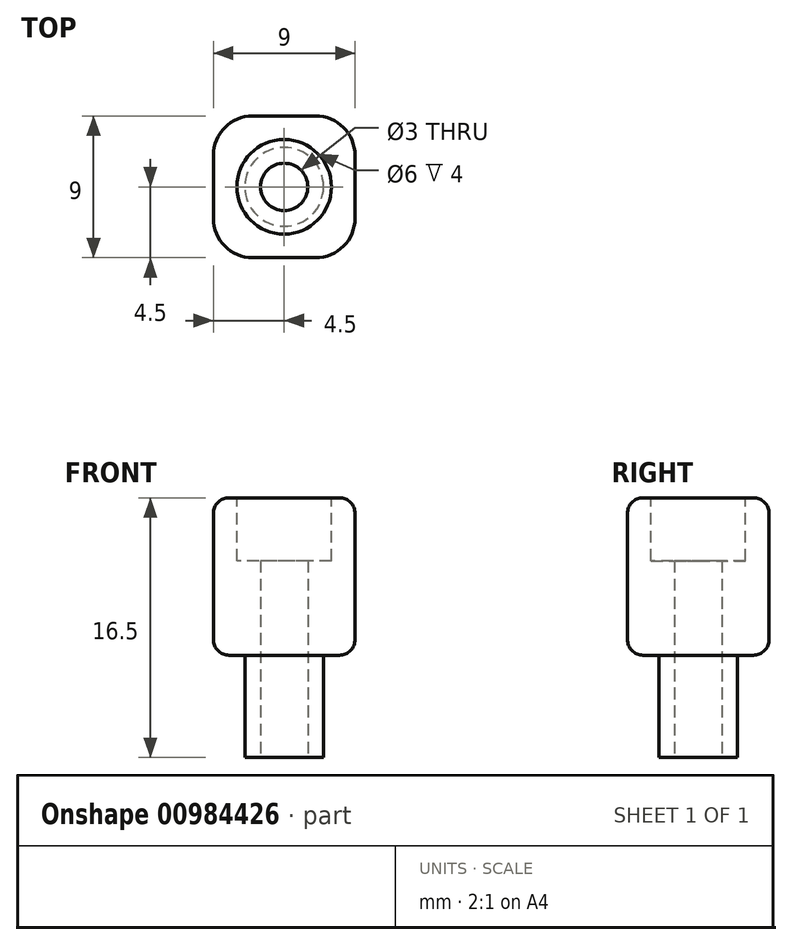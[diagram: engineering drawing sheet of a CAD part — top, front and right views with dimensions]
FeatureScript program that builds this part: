
annotation { "Feature Type Name" : "Feature", "Feature Type Description" : "" }
export const myFeature = defineFeature(function(context is Context, id is Id, definition is map)
    precondition{}
    {
        {
            var Q0;
            Q0=qCreatedBy(makeId("Top.planeOp"),FACE);
            var sketch = newSketch(context, id + "F0", { "sketchPlane" : qUnion([Q0])});
            skCircle(sketch, "E0", {"center": v(0, 0) * mm, "radius": 1.5 * mm});
            skCircle(sketch, "E1", {"center": v(0, 0) * mm, "radius": 2.5 * mm});
            skSolve(sketch);
        }
        {
            var Q0;
            Q0=makeQuery(id+"F0.imprint","IMPRINT",FACE,{"disambiguationData":[TD([[makeQuery(id+"F0.imprint","IMPRINT",EDGE,{"derivedFrom":sQuery(id+"F0.wireOp",EDGE,"E0")}),-1.0]])]});
            extrude(context, id + "F1", {"entities" : qUnion([Q0]), "depth" : 6.5 * mm, "offsetDistance" : 25 * mm});
        }
        {
            var Q0;
            Q0=makeQuery(id+"F1.opExtrude","CAP_FACE",FACE,{"disambiguationData":[OSD([sQuery(id+"F0.wireOp",EDGE,"E0"),sQuery(id+"F0.wireOp",EDGE,"E1")])],"isStart":false});
            var sketch = newSketch(context, id + "F2", { "sketchPlane" : qUnion([Q0])});
            skLineSegment(sketch, "E2.bottom", {"start": v(4.5, -4.5) * mm, "end": v(-4.5, -4.5) * mm});
            skLineSegment(sketch, "E2.top", {"start": v(4.5, 4.5) * mm, "end": v(-4.5, 4.5) * mm});
            skLineSegment(sketch, "E2.left", {"start": v(4.5, -4.5) * mm, "end": v(4.5, 4.5) * mm});
            skLineSegment(sketch, "E2.right", {"start": v(-4.5, -4.5) * mm, "end": v(-4.5, 4.5) * mm});
            skPoint(sketch, "E2.middle", {"position": v(0, 0) * mm});
            skSolve(sketch);
        }
        {
            var Q0;
            Q0 = qSketchRegion(id + "F2", true);
            extrude(context, id + "F3", {"entities" : qUnion([Q0]), "operationType" : NewBodyOperationType.ADD, "depth" : 10 * mm, "offsetDistance" : 25 * mm});
        }
        {
            var Q0;
            Q0=makeQuery(id+"F3.opExtrude","SWEPT_EDGE",EDGE,{"disambiguationData":[OSD([sQuery(id+"F2.wireOp",EDGE,"E2.bottom"),sQuery(id+"F2.wireOp",EDGE,"E2.right")])]});
            var Q1;
            Q1=makeQuery(id+"F3.opExtrude","SWEPT_EDGE",EDGE,{"disambiguationData":[OSD([sQuery(id+"F2.wireOp",EDGE,"E2.bottom"),sQuery(id+"F2.wireOp",EDGE,"E2.left")])]});
            var Q2;
            Q2=makeQuery(id+"F3.opExtrude","SWEPT_EDGE",EDGE,{"disambiguationData":[OSD([sQuery(id+"F2.wireOp",EDGE,"E2.top"),sQuery(id+"F2.wireOp",EDGE,"E2.left")])]});
            var Q3;
            Q3=makeQuery(id+"F3.opExtrude","SWEPT_EDGE",EDGE,{"disambiguationData":[OSD([sQuery(id+"F2.wireOp",EDGE,"E2.top"),sQuery(id+"F2.wireOp",EDGE,"E2.right")])]});
            fillet(context, id + "F4", {"entities" : qUnion([Q0, Q1, Q2, Q3]), "radius" : 2.5 * mm, "tangentPropagation" : true, "allowEdgeOverflow" : false});
        }
        {
            var Q0;
            {var subQ0=sQuery(id+"F2.wireOp",EDGE,"E2.bottom");var subQ1=sQuery(id+"F2.wireOp",EDGE,"E2.right");Q0=makeQuery(id+"F3.boolean.opBoolean","SPLIT",EDGE,{"disambiguationData":[TD([makeQuery(id+"F3.opExtrude","SWEPT_FACE",FACE,{"disambiguationData":[OSD([subQ0])]})])],"derivedFrom":makeQuery(id+"F3.opExtrude","CAP_EDGE",EDGE,{"disambiguationData":[OSD([subQ1])],"isStart":true})});}
            var Q1;
            Q1=makeQuery(id+"F3.opExtrude","CAP_EDGE",EDGE,{"disambiguationData":[OSD([sQuery(id+"F2.wireOp",EDGE,"E2.right")])],"isStart":false});
            fillet(context, id + "F5", {"entities" : qUnion([Q0, Q1]), "radius" : 1 * mm, "tangentPropagation" : true, "allowEdgeOverflow" : false});
        }
        {
            var Q0;
            Q0=makeQuery(id+"F3.boolean.opBoolean","SPLIT",FACE,{"disambiguationData":[TD([makeQuery(id+"F1.opExtrude","SWEPT_FACE",FACE,{"disambiguationData":[OSD([sQuery(id+"F0.wireOp",EDGE,"E0")])]})])],"derivedFrom":makeQuery(id+"F3.opExtrude","CAP_FACE",FACE,{"disambiguationData":[OSD([sQuery(id+"F2.wireOp",EDGE,"E2.bottom"),sQuery(id+"F2.wireOp",EDGE,"E2.top"),sQuery(id+"F2.wireOp",EDGE,"E2.left"),sQuery(id+"F2.wireOp",EDGE,"E2.right")])],"isStart":true})});
            extrude(context, id + "F6", {"entities" : qUnion([Q0]), "operationType" : NewBodyOperationType.REMOVE, "oppositeDirection" : true, "depth" : 10 * mm, "offsetDistance" : 25 * mm});
        }
        {
            var Q0;
            Q0=makeQuery(id+"F3.opExtrude","CAP_FACE",FACE,{"disambiguationData":[OSD([sQuery(id+"F2.wireOp",EDGE,"E2.bottom"),sQuery(id+"F2.wireOp",EDGE,"E2.top"),sQuery(id+"F2.wireOp",EDGE,"E2.left"),sQuery(id+"F2.wireOp",EDGE,"E2.right")])],"isStart":false});
            var sketch = newSketch(context, id + "F7", { "sketchPlane" : qUnion([Q0])});
            skCircle(sketch, "E3", {"center": v(0, 0) * mm, "radius": 3 * mm});
            skSolve(sketch);
        }
        {
            var Q0;
            Q0 = qSketchRegion(id + "F7", true);
            extrude(context, id + "F8", {"entities" : qUnion([Q0]), "operationType" : NewBodyOperationType.REMOVE, "oppositeDirection" : true, "depth" : 4 * mm, "offsetDistance" : 25 * mm});
        }
    });
